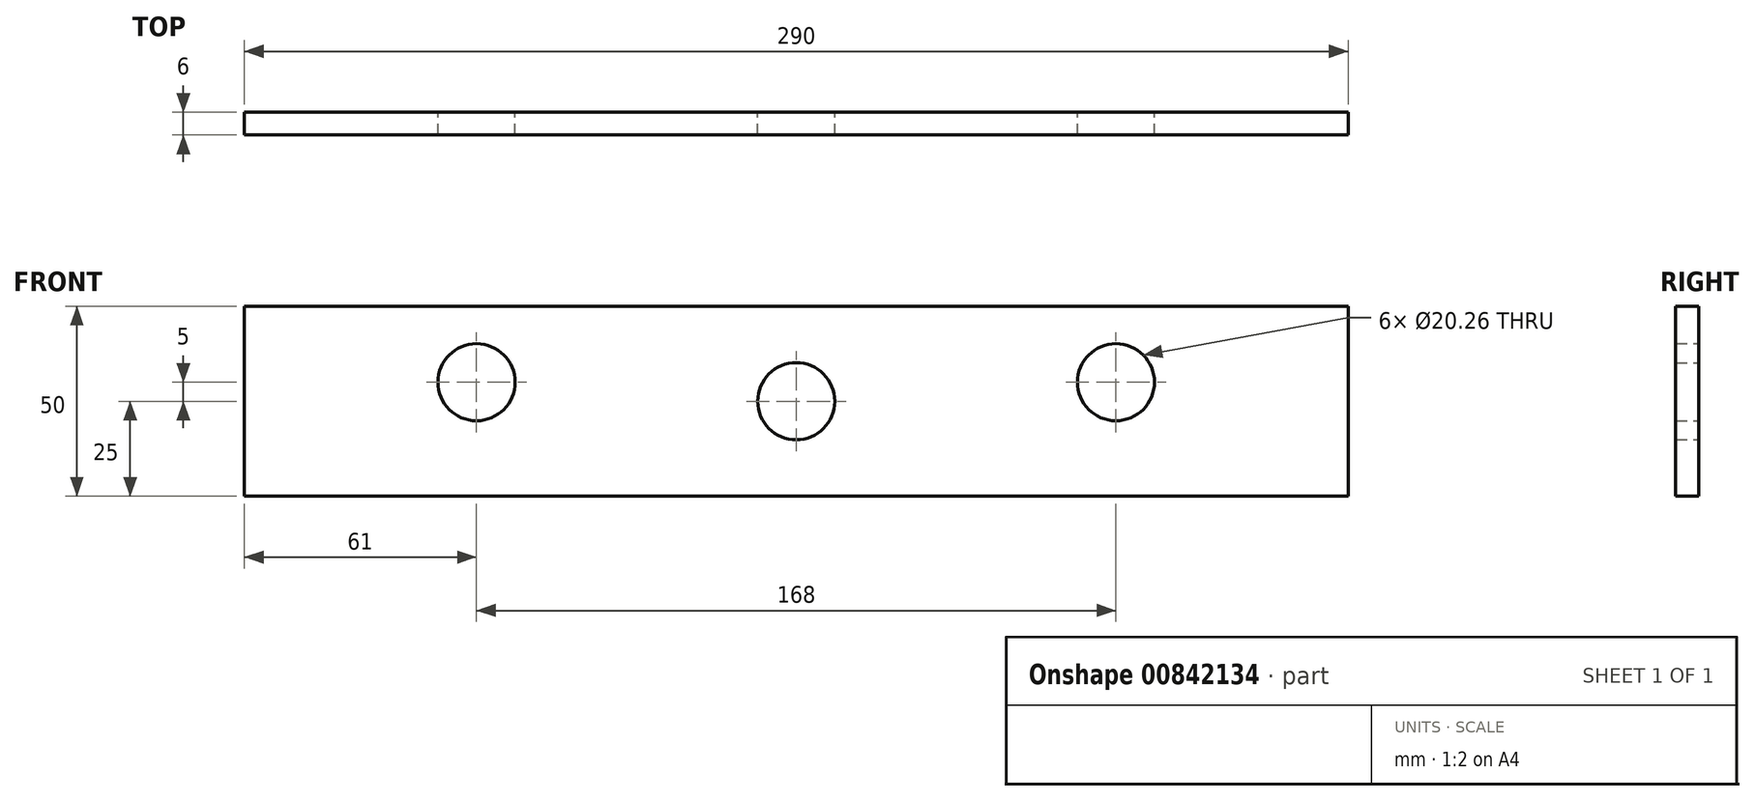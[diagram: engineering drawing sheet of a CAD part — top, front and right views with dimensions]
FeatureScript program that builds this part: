
annotation { "Feature Type Name" : "Feature", "Feature Type Description" : "" }
export const myFeature = defineFeature(function(context is Context, id is Id, definition is map)
    precondition{}
    {
        {
            var Q0;
            Q0=qCreatedBy(makeId("Front.planeOp"),FACE);
            var sketch = newSketch(context, id + "F0", { "sketchPlane" : qUnion([Q0])});
            skLineSegment(sketch, "E0.bottom", {"start": v(145, 25) * mm, "end": v(-145, 25) * mm});
            skLineSegment(sketch, "E0.top", {"start": v(145, -25) * mm, "end": v(-145, -25) * mm});
            skLineSegment(sketch, "E0.left", {"start": v(145, 25) * mm, "end": v(145, -25) * mm});
            skLineSegment(sketch, "E0.right", {"start": v(-145, 25) * mm, "end": v(-145, -25) * mm});
            skPoint(sketch, "E0.middle", {"position": v(0, 0) * mm});
            skCircle(sketch, "E1", {"center": v(0, 0) * mm, "radius": 10.13 * mm});
            skCircle(sketch, "E2", {"center": v(84, 5) * mm, "radius": 10.13 * mm});
            skCircle(sketch, "E3", {"center": v(-84, 5) * mm, "radius": 10.13 * mm});
            skSolve(sketch);
        }
        {
            var Q0;
            Q0=makeQuery(id+"F0.imprint","IMPRINT",FACE,{"disambiguationData":[TD([[makeQuery(id+"F0.imprint","IMPRINT",EDGE,{"derivedFrom":sQuery(id+"F0.wireOp",EDGE,"E0.bottom")}),1.0]])]});
            extrude(context, id + "F1", {"entities" : qUnion([Q0]), "depth" : 6 * mm, "offsetDistance" : 25 * mm});
        }
    });
